annotation { "Feature Type Name" : "Feature", "Feature Type Description" : "" }
export const myFeature = defineFeature(function(context is Context, id is Id, definition is map)
    precondition{}
    {
        {
            var Q0;
            Q0=qCreatedBy(makeId("Top.planeOp"),FACE);
            var sketch = newSketch(context, id + "F0", { "sketchPlane" : qUnion([Q0])});
            skLineSegment(sketch, "E0.bottom", {"start": v(-292.1, -146.05) * mm, "end": v(292.1, -146.05) * mm});
            skLineSegment(sketch, "E0.top", {"start": v(-292.1, 146.05) * mm, "end": v(292.1, 146.05) * mm});
            skLineSegment(sketch, "E0.left", {"start": v(-292.1, -146.05) * mm, "end": v(-292.1, 146.05) * mm});
            skLineSegment(sketch, "E0.right", {"start": v(292.1, -146.05) * mm, "end": v(292.1, 146.05) * mm});
            skPoint(sketch, "E0.middle", {"position": v(0, 0) * mm});
            skLineSegment(sketch, "E1", {"start": v(0, 146.05) * mm, "end": v(0, -146.05) * mm, "construction": true});
            skLineSegment(sketch, "E2", {"start": v(-292.1, 121.76) * mm, "end": v(292.1, 121.76) * mm, "construction": true});
            skText(sketch, "E3", { "text": "SAHIR JAGGI", "fontName": "OpenSans-Regular.ttf"});
            skLineSegment(sketch, "E4", {"start": v(-292.1, 95.25) * mm, "end": v(292.1, 95.25) * mm, "construction": true});
            skText(sketch, "E5", { "text": "philosopher. mentor. friend.", "fontName": "OpenSans-Regular.ttf"});
            skLineSegment(sketch, "E6", {"start": v(-292.1, 44.45) * mm, "end": v(292.1, 44.45) * mm, "construction": true});
            const initialGuessF0  = {"E3": [-0.07213, 0.12176, 1, 0, 0.01825], "E5": [-0.16704, 0.09525, 1, 0, 0.01825]};
            skSetInitialGuess(sketch, initialGuessF0);
            skSolve(sketch);
        }
        {
            var Q0;
            Q0 = qSketchRegion(id + "F0", true);
            extrude(context, id + "F1", {"entities" : qUnion([Q0]), "depth" : 25.4 * mm});
        }
    });